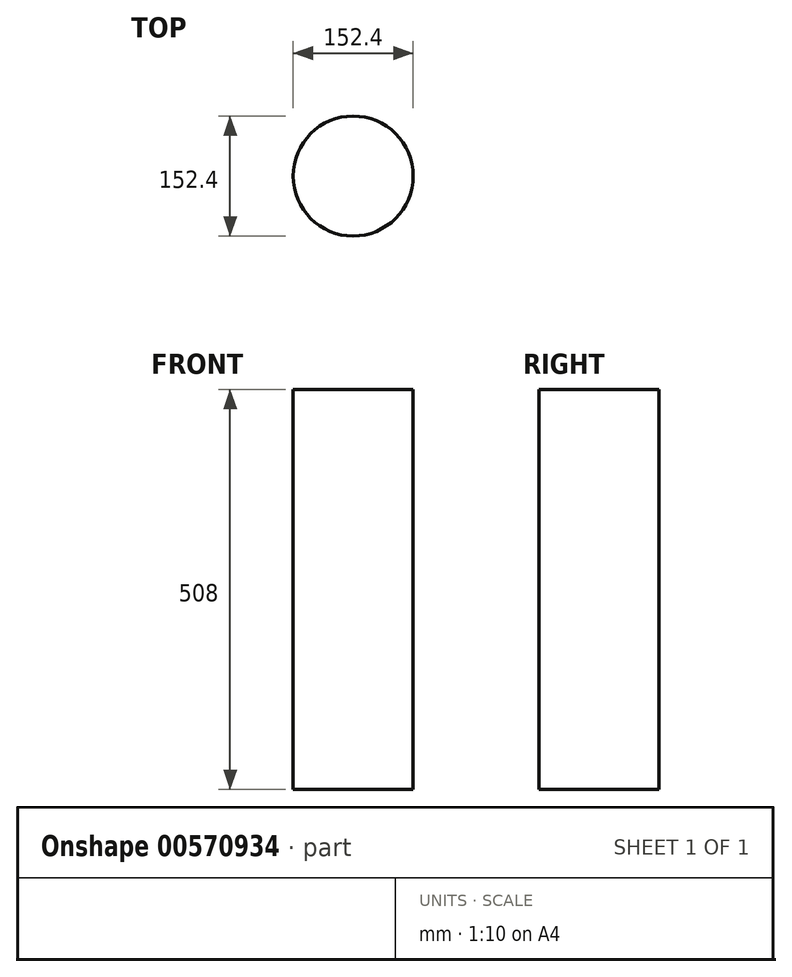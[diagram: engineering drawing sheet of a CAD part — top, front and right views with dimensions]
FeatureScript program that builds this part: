
annotation { "Feature Type Name" : "Feature", "Feature Type Description" : "" }
export const myFeature = defineFeature(function(context is Context, id is Id, definition is map)
    precondition{}
    {
        {
            var Q0;
            Q0=qCreatedBy(makeId("Top.planeOp"),FACE);
            var sketch = newSketch(context, id + "F0", { "sketchPlane" : qUnion([Q0])});
            skCircle(sketch, "E0", {"center": v(0, 0) * mm, "radius": 76.2 * mm});
            skSolve(sketch);
        }
        {
            var Q0;
            Q0 = qSketchRegion(id + "F0", true);
            extrude(context, id + "F1", {"entities" : qUnion([Q0]), "depth" : 508 * mm, "offsetDistance" : 25.4 * mm});
        }
    });
